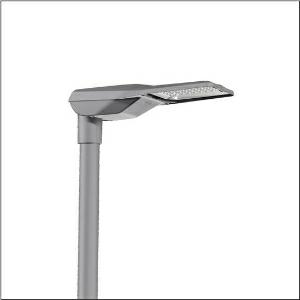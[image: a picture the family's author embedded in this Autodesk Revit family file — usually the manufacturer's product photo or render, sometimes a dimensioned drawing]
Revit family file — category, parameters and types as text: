
# Revit family: streetlight_sl_21_iq_mini___st1_0a_5xe2d41d08hb_6636
name_source: partatom
category: Lighting Fixtures
units: mm (PartAtom-declared; Revit-internal decimal feet)

## family parameters
Cut with Voids When Loaded = No
Host = Face
Light Source = No
Part Type = Normal
Room Calculation Point = No
Round Connector Dimension = Use Diameter
Shared = No

## types (1)
- --- (1 x LED, 9860 lm, 70.9 W, 4000K)
    Apparent Load = 71 VA
    CIE Flux Codes = 37 72 97 100 100
    Color Rendering = 70
    Color Temperature = 4000K
    Default Elevation = 1800 mm
    Description = Streetlight SL 21 iQ mini, mast luminaire, primary light control with lens, of PMMA, primary optical cover: cover, of toughened safety glass, transparent, light distribution: ST1.0a, light emission: direct distribution, primary light characteristic: asymmetric, installation type: post-top, side-entry, LED, High Power LED, rated luminous flux: 9.860lm, luminous efficacy: 139lm/W, light colour: 740, colour temperature: 4000K, control gear: iQ-Comfort, control: Auto-Match, Temp-Guard, Lumen-Switch, Night-Set, Smart-Wire, Light-Fading, Desk-Remote (wireless, voltage-free reading and setting of iQ features in the workshop via application-optimized NFC function/RFID function), optimised constant luminous flux control (CLO 2.0), pre-setting: linear dimming characteristic, mains connection: 220..240V, AC, 50/60Hz, start of lifetime: 71W, end of service life: 75W, reduction: 31W, luminaire housing, of diecast aluminium, powder-coated, Siteco® metallic grey (DB 702S), corrosivity category C5 mid according to DIN EN ISO 12944, please order mast flange separately, inclination adjustable: 0°, 5°, 10°, 15°, sealing non-destructively replaceable, multi-level sealing system, length: 628mm, width: 235mm, height: 110mm, mast flange for spigot size: 42mm (side-entry): 5XC10008XM4, 60/48mm (side-entry/post-top): 5XC10108XM2, 76/60mm (side-entry/post-top): 5XC10108XM1, mounting height: 4..8m, protection rating (complete): IP66, insulation class (complete): insulation class II (safety insulation), certification: CE, ENEC, ENEC+, VDE, impact resistance: IK10, permissible operating ambient temperature for outdoor applications: -40..+50°C, standard-compliant lighting for roads and squares, packaging unit: 1 piece

Light Distribution: ST1.0a
    Height = 110 mm
    Lamp = 1 x LED
    Lamp Light Flux = 9860 lm
    Lamp Power = 70.9 W
    Lamp count = 1
    Length = 625 mm
    Luminous efficacy = 139 lm/W
    Manufacturer = Siteco
    ModVariant = No
    Model = 5XE2D41D08HB
    Number of Poles = 1
    OnlyDefault = Yes
    Power Factor = 1
    Product Name = Streetlight SL 21 iQ mini | ST1.0a
    Product group = mast luminaire | pylon top
    ProductGroupID = 6100
    Protection Class = Protection class II
    Protection Degree = IP 66
    RLX_Detail_Level = 1
    RLX_Emergency_Light_Flux = 0 lm
    RLX_Emergency_Type = 0
    RLX_Emergency_Type_DB = No
    RlxData = <blob elided: 26277 chars, md5=c1de1b34>
    Socket = socket
    Standby Power = 0 W
    System Light Flux = 9860 lm
    System Power = 71 W
    Type Comments = factory setting: luminous flux: 100 % | dim-lin: 254 | 711 mA
    Type Image = l_1003519.jpg
    URL = http://relux.com
    VarID = @adj_179553
    Voltage = 0 V
    Weight = 0.00 kg
    Width = 234 mm

## geometry (parser evidence)
native form markers: Blend x4, Sweep x9
no freeform markers — native parametric forms only
